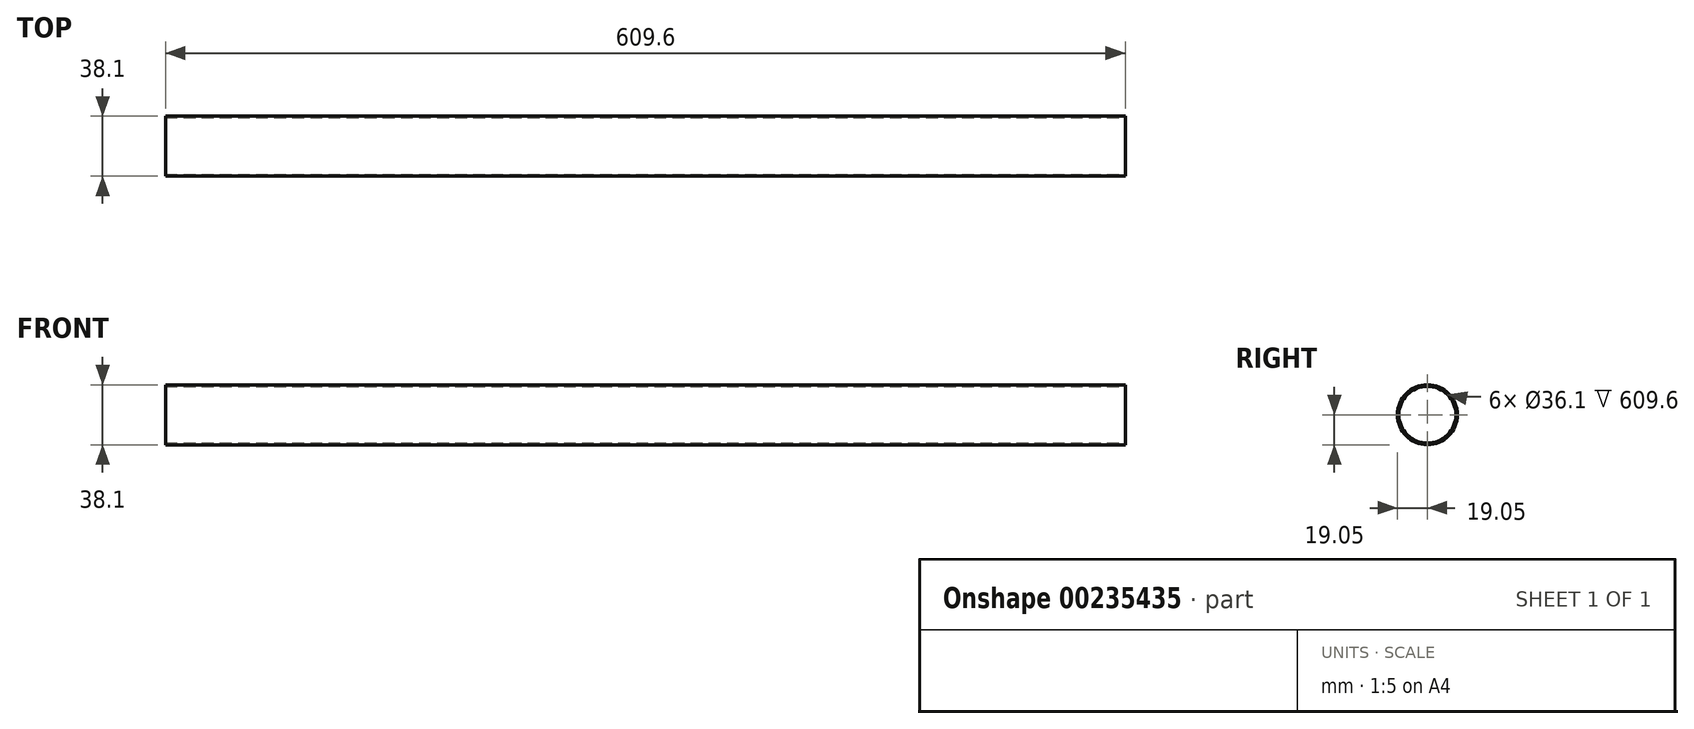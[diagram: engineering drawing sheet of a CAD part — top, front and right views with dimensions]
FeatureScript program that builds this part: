
annotation { "Feature Type Name" : "Feature", "Feature Type Description" : "" }
export const myFeature = defineFeature(function(context is Context, id is Id, definition is map)
    precondition{}
    {
        {
            var Q0;
            Q0=qCreatedBy(makeId("Top.planeOp"),FACE);
            var sketch = newSketch(context, id + "F0", { "sketchPlane" : qUnion([Q0])});
            skArc(sketch, "E0", {"start": v(304.8, 0) * mm, "mid": v(0, 19.98) * mm, "end": v(-304.8, 0) * mm, "construction": true});
            skLineSegment(sketch, "E1", {"start": v(-304.8, 0) * mm, "end": v(304.8, 0) * mm});
            skLineSegment(sketch, "E2", {"start": v(-304.8, 0) * mm, "end": v(0, -2315.19) * mm, "construction": true});
            skLineSegment(sketch, "E3", {"start": v(0, -2315.19) * mm, "end": v(304.8, 0) * mm, "construction": true});
            skSolve(sketch);
        }
        {
            var Q0;
            Q0=sQuery(id+"F0.wireOp",VERTEX,"E2.start");
            var Q1;
            Q1=sQuery(id+"F0.wireOp",EDGE,"E1");
            cPlane(context, id + "F1", {"entities" : qUnion([Q0, Q1]), "cplaneType" : CPlaneType.CURVE_POINT, "offset" : 25.4 * mm, "width" : 152.4 * mm, "height" : 152.4 * mm});
        }
        {
            var Q0;
            Q0=qCreatedBy(id+"F1.planeOp",FACE);
            var sketch = newSketch(context, id + "F2", { "sketchPlane" : qUnion([Q0])});
            skCircle(sketch, "E4", {"center": v(0, 0) * mm, "radius": 19.05 * mm});
            skCircle(sketch, "E5", {"center": v(0, 0) * mm, "radius": 18.05 * mm});
            skSolve(sketch);
        }
        {
            var Q0;
            Q0=makeQuery(id+"F2.imprint","IMPRINT",FACE,{"disambiguationData":[TD([[makeQuery(id+"F2.imprint","IMPRINT",EDGE,{"derivedFrom":sQuery(id+"F2.wireOp",EDGE,"E4")}),1.0]])]});
            var Q1;
            Q1=sQuery(id+"F0.wireOp",EDGE,"E1");
            sweep(context, id + "F3", {"profiles" : qUnion([Q0]), "path" : qUnion([Q1])});
        }
    });
